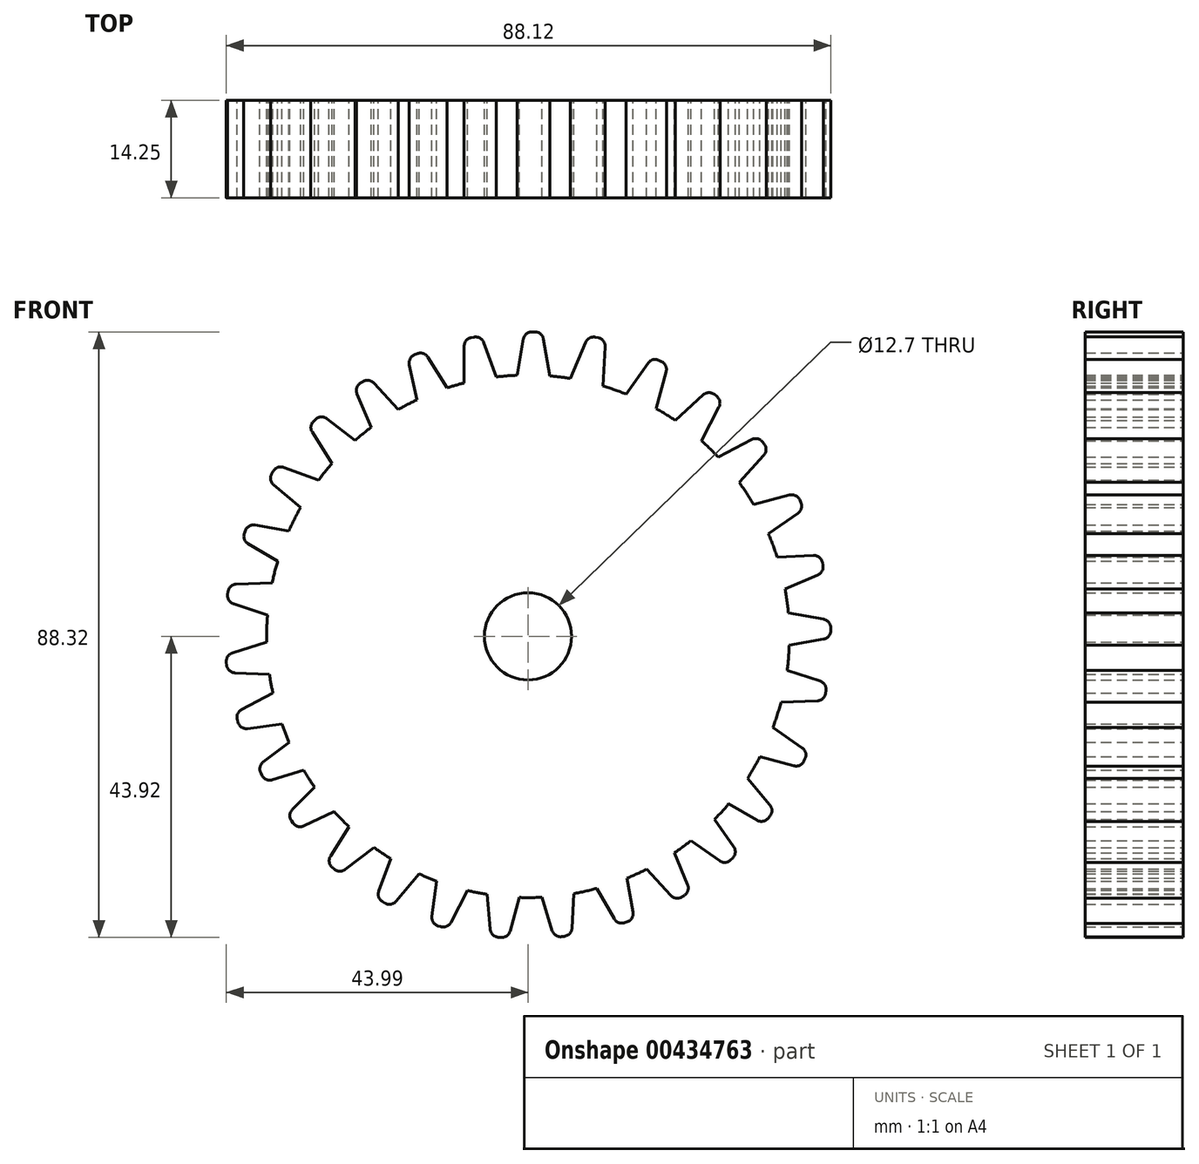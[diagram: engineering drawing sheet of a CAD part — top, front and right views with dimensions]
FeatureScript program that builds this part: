
annotation { "Feature Type Name" : "Feature", "Feature Type Description" : "" }
export const myFeature = defineFeature(function(context is Context, id is Id, definition is map)
    precondition{}
    {
        {
            var Q0;
            Q0=qCreatedBy(makeId("Front.planeOp"),FACE);
            var sketch = newSketch(context, id + "F0", { "sketchPlane" : qUnion([Q0])});
            skCircle(sketch, "E0", {"center": v(0, 0) * mm, "radius": 38.1 * mm});
            skCircle(sketch, "E1", {"center": v(0, 0) * mm, "radius": 6.35 * mm});
            skSolve(sketch);
        }
        {
            var Q0;
            Q0=makeQuery(id+"F0.imprint","IMPRINT",FACE,{"disambiguationData":[TD([[makeQuery(id+"F0.imprint","IMPRINT",EDGE,{"derivedFrom":sQuery(id+"F0.wireOp",EDGE,"E0")}),1.0]])]});
            extrude(context, id + "F1", {"entities" : qUnion([Q0]), "depth" : 7.87 * mm});
        }
        {
            var Q0;
            Q0=qCreatedBy(makeId("Front.planeOp"),FACE);
            var sketch = newSketch(context, id + "F2", { "sketchPlane" : qUnion([Q0])});
            skLineSegment(sketch, "E2", {"start": v(-58, 24.58) * mm, "end": v(-57.59, 24.58) * mm});
            skLineSegment(sketch, "E3", {"start": v(-56.34, 23.53) * mm, "end": v(-55.23, 17.27) * mm});
            skLineSegment(sketch, "E4", {"start": v(-55.23, 17.27) * mm, "end": v(-60.35, 17.27) * mm});
            skLineSegment(sketch, "E5", {"start": v(-59.25, 23.53) * mm, "end": v(-60.35, 17.27) * mm});
            skPoint(sketch, "E6.visualSharp", {"position": v(-59.06, 24.58) * mm});
            skArc(sketch, "E6.filletArc", {"start": v(-58, 24.58) * mm, "mid": v(-58.81, 24.29) * mm, "end": v(-59.25, 23.53) * mm});
            skPoint(sketch, "E7.visualSharp", {"position": v(-56.52, 24.58) * mm});
            skArc(sketch, "E7.filletArc", {"start": v(-56.34, 23.53) * mm, "mid": v(-56.77, 24.29) * mm, "end": v(-57.59, 24.58) * mm});
            skLineSegment(sketch, "E8", {"start": v(9.87, 43.61) * mm, "end": v(10.27, 43.52) * mm});
            skLineSegment(sketch, "E9", {"start": v(11.25, 42.22) * mm, "end": v(10.92, 35.86) * mm});
            skLineSegment(sketch, "E10", {"start": v(10.92, 35.86) * mm, "end": v(5.93, 37.01) * mm});
            skLineSegment(sketch, "E11", {"start": v(8.42, 42.87) * mm, "end": v(5.93, 37.01) * mm});
            skArc(sketch, "E12.filletArc", {"start": v(9.87, 43.61) * mm, "mid": v(9, 43.5) * mm, "end": v(8.42, 42.87) * mm});
            skArc(sketch, "E13.filletArc", {"start": v(11.25, 42.22) * mm, "mid": v(11, 43.05) * mm, "end": v(10.27, 43.52) * mm});
            skLineSegment(sketch, "E14", {"start": v(19.08, 40.25) * mm, "end": v(19.45, 40.08) * mm});
            skLineSegment(sketch, "E15", {"start": v(20.13, 38.6) * mm, "end": v(18.44, 32.46) * mm});
            skLineSegment(sketch, "E16", {"start": v(18.44, 32.46) * mm, "end": v(13.81, 34.66) * mm});
            skLineSegment(sketch, "E17", {"start": v(17.5, 39.84) * mm, "end": v(13.81, 34.66) * mm});
            skArc(sketch, "E18.filletArc", {"start": v(19.08, 40.25) * mm, "mid": v(18.21, 40.34) * mm, "end": v(17.5, 39.84) * mm});
            skArc(sketch, "E19.filletArc", {"start": v(20.13, 38.6) * mm, "mid": v(20.06, 39.46) * mm, "end": v(19.45, 40.08) * mm});
            skLineSegment(sketch, "E20", {"start": v(27.15, 35.27) * mm, "end": v(27.48, 35.03) * mm});
            skLineSegment(sketch, "E21", {"start": v(27.84, 33.43) * mm, "end": v(24.91, 27.78) * mm});
            skLineSegment(sketch, "E22", {"start": v(24.91, 27.78) * mm, "end": v(20.84, 30.88) * mm});
            skLineSegment(sketch, "E23", {"start": v(25.52, 35.2) * mm, "end": v(20.84, 30.88) * mm});
            skArc(sketch, "E24.filletArc", {"start": v(27.15, 35.27) * mm, "mid": v(26.32, 35.53) * mm, "end": v(25.52, 35.2) * mm});
            skArc(sketch, "E25.filletArc", {"start": v(27.84, 33.43) * mm, "mid": v(27.95, 34.3) * mm, "end": v(27.48, 35.03) * mm});
            skLineSegment(sketch, "E26", {"start": v(34.19, 28.35) * mm, "end": v(34.44, 28.03) * mm});
            skLineSegment(sketch, "E27", {"start": v(34.38, 26.4) * mm, "end": v(30.1, 21.68) * mm});
            skLineSegment(sketch, "E28", {"start": v(30.1, 21.68) * mm, "end": v(26.97, 25.73) * mm});
            skLineSegment(sketch, "E29", {"start": v(32.6, 28.7) * mm, "end": v(26.97, 25.73) * mm});
            skArc(sketch, "E30.filletArc", {"start": v(34.19, 28.35) * mm, "mid": v(33.45, 28.82) * mm, "end": v(32.6, 28.7) * mm});
            skArc(sketch, "E31.filletArc", {"start": v(34.38, 26.4) * mm, "mid": v(34.7, 27.2) * mm, "end": v(34.44, 28.03) * mm});
            skLineSegment(sketch, "E32", {"start": v(39.6, 19.9) * mm, "end": v(39.77, 19.53) * mm});
            skLineSegment(sketch, "E33", {"start": v(39.35, 17.96) * mm, "end": v(34.14, 14.3) * mm});
            skLineSegment(sketch, "E34", {"start": v(34.14, 14.3) * mm, "end": v(31.97, 18.95) * mm});
            skLineSegment(sketch, "E35", {"start": v(38.12, 20.6) * mm, "end": v(31.97, 18.95) * mm});
            skArc(sketch, "E36.filletArc", {"start": v(39.6, 19.9) * mm, "mid": v(38.98, 20.52) * mm, "end": v(38.12, 20.6) * mm});
            skArc(sketch, "E37.filletArc", {"start": v(39.35, 17.96) * mm, "mid": v(39.85, 18.67) * mm, "end": v(39.77, 19.53) * mm});
            skLineSegment(sketch, "E38", {"start": v(42.9, 10.8) * mm, "end": v(43, 10.4) * mm});
            skLineSegment(sketch, "E39", {"start": v(42.25, 8.95) * mm, "end": v(36.4, 6.47) * mm});
            skLineSegment(sketch, "E40", {"start": v(36.4, 6.47) * mm, "end": v(35.24, 11.46) * mm});
            skLineSegment(sketch, "E41", {"start": v(41.6, 11.79) * mm, "end": v(35.24, 11.46) * mm});
            skArc(sketch, "E42.filletArc", {"start": v(42.9, 10.8) * mm, "mid": v(42.43, 11.53) * mm, "end": v(41.6, 11.79) * mm});
            skArc(sketch, "E43.filletArc", {"start": v(42.25, 8.95) * mm, "mid": v(42.89, 9.54) * mm, "end": v(43, 10.4) * mm});
            skLineSegment(sketch, "E44", {"start": v(44.13, 1.24) * mm, "end": v(44.13, 0.83) * mm});
            skLineSegment(sketch, "E45", {"start": v(43.08, -0.42) * mm, "end": v(36.82, -1.52) * mm});
            skLineSegment(sketch, "E46", {"start": v(36.82, -1.52) * mm, "end": v(36.82, 3.6) * mm});
            skLineSegment(sketch, "E47", {"start": v(43.08, 2.5) * mm, "end": v(36.82, 3.6) * mm});
            skArc(sketch, "E48.filletArc", {"start": v(44.13, 1.24) * mm, "mid": v(43.84, 2.06) * mm, "end": v(43.08, 2.5) * mm});
            skArc(sketch, "E49.filletArc", {"start": v(43.08, -0.42) * mm, "mid": v(43.84, 0.02) * mm, "end": v(44.13, 0.83) * mm});
            skLineSegment(sketch, "E50", {"start": v(43.43, -7.9) * mm, "end": v(43.38, -8.31) * mm});
            skLineSegment(sketch, "E51", {"start": v(42.17, -9.4) * mm, "end": v(35.8, -9.64) * mm});
            skLineSegment(sketch, "E52", {"start": v(35.8, -9.64) * mm, "end": v(36.51, -4.57) * mm});
            skLineSegment(sketch, "E53", {"start": v(42.57, -6.52) * mm, "end": v(36.51, -4.57) * mm});
            skArc(sketch, "E54.filletArc", {"start": v(43.43, -7.9) * mm, "mid": v(43.25, -7.06) * mm, "end": v(42.57, -6.52) * mm});
            skArc(sketch, "E55.filletArc", {"start": v(42.17, -9.4) * mm, "mid": v(42.97, -9.08) * mm, "end": v(43.38, -8.31) * mm});
            skLineSegment(sketch, "E56", {"start": v(40.4, -17.82) * mm, "end": v(40.22, -18.2) * mm});
            skLineSegment(sketch, "E57", {"start": v(38.74, -18.88) * mm, "end": v(32.6, -17.24) * mm});
            skLineSegment(sketch, "E58", {"start": v(32.6, -17.24) * mm, "end": v(34.76, -12.6) * mm});
            skLineSegment(sketch, "E59", {"start": v(39.97, -16.25) * mm, "end": v(34.76, -12.6) * mm});
            skArc(sketch, "E60.filletArc", {"start": v(40.4, -17.82) * mm, "mid": v(40.47, -16.96) * mm, "end": v(39.97, -16.25) * mm});
            skArc(sketch, "E61.filletArc", {"start": v(38.74, -18.88) * mm, "mid": v(39.6, -18.8) * mm, "end": v(40.22, -18.2) * mm});
            skLineSegment(sketch, "E62", {"start": v(35.25, -26.23) * mm, "end": v(35, -26.54) * mm});
            skLineSegment(sketch, "E63", {"start": v(33.38, -26.82) * mm, "end": v(27.87, -23.64) * mm});
            skLineSegment(sketch, "E64", {"start": v(27.87, -23.64) * mm, "end": v(31.16, -19.72) * mm});
            skLineSegment(sketch, "E65", {"start": v(35.25, -24.6) * mm, "end": v(31.16, -19.72) * mm});
            skArc(sketch, "E66.filletArc", {"start": v(35.25, -26.23) * mm, "mid": v(35.55, -25.4) * mm, "end": v(35.25, -24.6) * mm});
            skArc(sketch, "E67.filletArc", {"start": v(33.38, -26.82) * mm, "mid": v(34.24, -26.97) * mm, "end": v(35, -26.54) * mm});
            skLineSegment(sketch, "E68", {"start": v(29.84, -32.3) * mm, "end": v(29.55, -32.6) * mm});
            skLineSegment(sketch, "E69", {"start": v(27.92, -32.74) * mm, "end": v(22.71, -29.1) * mm});
            skLineSegment(sketch, "E70", {"start": v(22.71, -29.1) * mm, "end": v(26.33, -25.47) * mm});
            skLineSegment(sketch, "E71", {"start": v(29.98, -30.68) * mm, "end": v(26.33, -25.47) * mm});
            skArc(sketch, "E72.filletArc", {"start": v(29.84, -32.3) * mm, "mid": v(30.2, -31.52) * mm, "end": v(29.98, -30.68) * mm});
            skArc(sketch, "E73.filletArc", {"start": v(27.92, -32.74) * mm, "mid": v(28.76, -32.97) * mm, "end": v(29.55, -32.6) * mm});
            skLineSegment(sketch, "E74", {"start": v(22.78, -37.77) * mm, "end": v(22.44, -38) * mm});
            skLineSegment(sketch, "E75", {"start": v(20.82, -37.78) * mm, "end": v(16.5, -33.11) * mm});
            skLineSegment(sketch, "E76", {"start": v(16.5, -33.11) * mm, "end": v(20.8, -30.34) * mm});
            skLineSegment(sketch, "E77", {"start": v(23.27, -36.21) * mm, "end": v(20.8, -30.34) * mm});
            skArc(sketch, "E78.filletArc", {"start": v(22.78, -37.77) * mm, "mid": v(23.3, -37.08) * mm, "end": v(23.27, -36.21) * mm});
            skArc(sketch, "E79.filletArc", {"start": v(20.82, -37.78) * mm, "mid": v(21.6, -38.18) * mm, "end": v(22.44, -38) * mm});
            skLineSegment(sketch, "E80", {"start": v(14.49, -41.62) * mm, "end": v(14.1, -41.76) * mm});
            skLineSegment(sketch, "E81", {"start": v(12.57, -41.2) * mm, "end": v(9.4, -35.68) * mm});
            skLineSegment(sketch, "E82", {"start": v(9.4, -35.68) * mm, "end": v(14.21, -33.94) * mm});
            skLineSegment(sketch, "E83", {"start": v(15.3, -40.2) * mm, "end": v(14.21, -33.94) * mm});
            skArc(sketch, "E84.filletArc", {"start": v(14.49, -41.62) * mm, "mid": v(15.16, -41.06) * mm, "end": v(15.3, -40.2) * mm});
            skArc(sketch, "E85.filletArc", {"start": v(12.57, -41.2) * mm, "mid": v(13.24, -41.75) * mm, "end": v(14.1, -41.76) * mm});
            skLineSegment(sketch, "E86", {"start": v(5.3, -43.74) * mm, "end": v(4.89, -43.8) * mm});
            skLineSegment(sketch, "E87", {"start": v(3.52, -42.91) * mm, "end": v(1.63, -36.84) * mm});
            skLineSegment(sketch, "E88", {"start": v(1.63, -36.84) * mm, "end": v(6.7, -36.19) * mm});
            skLineSegment(sketch, "E89", {"start": v(6.4, -42.54) * mm, "end": v(6.7, -36.19) * mm});
            skArc(sketch, "E90.filletArc", {"start": v(5.3, -43.74) * mm, "mid": v(6.07, -43.35) * mm, "end": v(6.4, -42.54) * mm});
            skArc(sketch, "E91.filletArc", {"start": v(3.52, -42.91) * mm, "mid": v(4.04, -43.6) * mm, "end": v(4.89, -43.8) * mm});
            skLineSegment(sketch, "E92", {"start": v(-3.96, -43.91) * mm, "end": v(-4.37, -43.87) * mm});
            skLineSegment(sketch, "E93", {"start": v(-5.52, -42.71) * mm, "end": v(-6.04, -36.37) * mm});
            skLineSegment(sketch, "E94", {"start": v(-6.04, -36.37) * mm, "end": v(-0.95, -36.84) * mm});
            skLineSegment(sketch, "E95", {"start": v(-2.62, -42.98) * mm, "end": v(-0.95, -36.84) * mm});
            skArc(sketch, "E96.filletArc", {"start": v(-3.96, -43.91) * mm, "mid": v(-3.12, -43.69) * mm, "end": v(-2.62, -42.98) * mm});
            skArc(sketch, "E97.filletArc", {"start": v(-5.52, -42.71) * mm, "mid": v(-5.16, -43.5) * mm, "end": v(-4.37, -43.87) * mm});
            skLineSegment(sketch, "E98", {"start": v(-12.74, -42.34) * mm, "end": v(-13.13, -42.21) * mm});
            skLineSegment(sketch, "E99", {"start": v(-14.01, -40.84) * mm, "end": v(-13.18, -34.53) * mm});
            skLineSegment(sketch, "E100", {"start": v(-13.18, -34.53) * mm, "end": v(-8.3, -36.07) * mm});
            skLineSegment(sketch, "E101", {"start": v(-11.24, -41.71) * mm, "end": v(-8.3, -36.07) * mm});
            skArc(sketch, "E102.filletArc", {"start": v(-12.74, -42.34) * mm, "mid": v(-11.88, -42.3) * mm, "end": v(-11.24, -41.71) * mm});
            skArc(sketch, "E103.filletArc", {"start": v(-14.01, -40.84) * mm, "mid": v(-13.82, -41.68) * mm, "end": v(-13.13, -42.21) * mm});
            skLineSegment(sketch, "E104", {"start": v(-20.84, -38.92) * mm, "end": v(-21.2, -38.72) * mm});
            skLineSegment(sketch, "E105", {"start": v(-21.76, -37.18) * mm, "end": v(-19.59, -31.2) * mm});
            skLineSegment(sketch, "E106", {"start": v(-19.59, -31.2) * mm, "end": v(-15.15, -33.75) * mm});
            skLineSegment(sketch, "E107", {"start": v(-19.23, -38.63) * mm, "end": v(-15.15, -33.75) * mm});
            skArc(sketch, "E108.filletArc", {"start": v(-20.84, -38.92) * mm, "mid": v(-19.99, -39.07) * mm, "end": v(-19.23, -38.63) * mm});
            skArc(sketch, "E109.filletArc", {"start": v(-21.76, -37.18) * mm, "mid": v(-21.76, -38.05) * mm, "end": v(-21.2, -38.72) * mm});
            skLineSegment(sketch, "E110", {"start": v(-28.28, -33.93) * mm, "end": v(-28.58, -33.66) * mm});
            skLineSegment(sketch, "E111", {"start": v(-28.8, -32.04) * mm, "end": v(-25.37, -26.67) * mm});
            skLineSegment(sketch, "E112", {"start": v(-25.37, -26.67) * mm, "end": v(-21.6, -30.13) * mm});
            skLineSegment(sketch, "E113", {"start": v(-26.65, -34) * mm, "end": v(-21.6, -30.13) * mm});
            skArc(sketch, "E114.filletArc", {"start": v(-28.28, -33.93) * mm, "mid": v(-27.48, -34.27) * mm, "end": v(-26.65, -34) * mm});
            skArc(sketch, "E115.filletArc", {"start": v(-28.8, -32.04) * mm, "mid": v(-28.98, -32.89) * mm, "end": v(-28.58, -33.66) * mm});
            skLineSegment(sketch, "E116", {"start": v(-34.27, -27.22) * mm, "end": v(-34.5, -26.88) * mm});
            skLineSegment(sketch, "E117", {"start": v(-34.36, -25.26) * mm, "end": v(-29.86, -20.76) * mm});
            skLineSegment(sketch, "E118", {"start": v(-29.86, -20.76) * mm, "end": v(-26.92, -24.95) * mm});
            skLineSegment(sketch, "E119", {"start": v(-32.7, -27.64) * mm, "end": v(-26.92, -24.95) * mm});
            skArc(sketch, "E120.filletArc", {"start": v(-34.27, -27.22) * mm, "mid": v(-33.56, -27.72) * mm, "end": v(-32.7, -27.64) * mm});
            skArc(sketch, "E121.filletArc", {"start": v(-34.36, -25.26) * mm, "mid": v(-34.73, -26.05) * mm, "end": v(-34.5, -26.88) * mm});
            skLineSegment(sketch, "E122", {"start": v(-38.77, -20.3) * mm, "end": v(-38.95, -19.93) * mm});
            skLineSegment(sketch, "E123", {"start": v(-38.6, -18.34) * mm, "end": v(-33.54, -14.48) * mm});
            skLineSegment(sketch, "E124", {"start": v(-33.54, -14.48) * mm, "end": v(-31.19, -19.02) * mm});
            skLineSegment(sketch, "E125", {"start": v(-37.26, -20.92) * mm, "end": v(-31.19, -19.02) * mm});
            skArc(sketch, "E126.filletArc", {"start": v(-38.77, -20.3) * mm, "mid": v(-38.13, -20.88) * mm, "end": v(-37.26, -20.92) * mm});
            skArc(sketch, "E127.filletArc", {"start": v(-38.6, -18.34) * mm, "mid": v(-39.07, -19.07) * mm, "end": v(-38.95, -19.93) * mm});
            skLineSegment(sketch, "E128", {"start": v(-42.26, -12.59) * mm, "end": v(-42.38, -12.2) * mm});
            skLineSegment(sketch, "E129", {"start": v(-41.77, -10.69) * mm, "end": v(-36.14, -7.72) * mm});
            skLineSegment(sketch, "E130", {"start": v(-36.14, -7.72) * mm, "end": v(-34.57, -12.59) * mm});
            skLineSegment(sketch, "E131", {"start": v(-40.87, -13.46) * mm, "end": v(-34.57, -12.59) * mm});
            skArc(sketch, "E132.filletArc", {"start": v(-42.26, -12.59) * mm, "mid": v(-41.72, -13.28) * mm, "end": v(-40.87, -13.46) * mm});
            skArc(sketch, "E133.filletArc", {"start": v(-41.77, -10.69) * mm, "mid": v(-42.35, -11.33) * mm, "end": v(-42.38, -12.2) * mm});
            skLineSegment(sketch, "E134", {"start": v(-43.93, -4.22) * mm, "end": v(-43.98, -3.82) * mm});
            skLineSegment(sketch, "E135", {"start": v(-43.1, -2.44) * mm, "end": v(-37.03, -0.54) * mm});
            skLineSegment(sketch, "E136", {"start": v(-37.03, -0.54) * mm, "end": v(-36.37, -5.61) * mm});
            skLineSegment(sketch, "E137", {"start": v(-42.72, -5.33) * mm, "end": v(-36.37, -5.61) * mm});
            skArc(sketch, "E138.filletArc", {"start": v(-43.93, -4.22) * mm, "mid": v(-43.53, -5) * mm, "end": v(-42.72, -5.33) * mm});
            skArc(sketch, "E139.filletArc", {"start": v(-43.1, -2.44) * mm, "mid": v(-43.8, -2.97) * mm, "end": v(-43.98, -3.82) * mm});
            skLineSegment(sketch, "E140", {"start": v(-43.79, 6.1) * mm, "end": v(-43.73, 6.5) * mm});
            skLineSegment(sketch, "E141", {"start": v(-42.52, 7.6) * mm, "end": v(-36.16, 7.84) * mm});
            skLineSegment(sketch, "E142", {"start": v(-36.16, 7.84) * mm, "end": v(-36.86, 2.77) * mm});
            skLineSegment(sketch, "E143", {"start": v(-42.92, 4.72) * mm, "end": v(-36.86, 2.77) * mm});
            skArc(sketch, "E144.filletArc", {"start": v(-43.79, 6.1) * mm, "mid": v(-43.6, 5.25) * mm, "end": v(-42.92, 4.72) * mm});
            skArc(sketch, "E145.filletArc", {"start": v(-42.52, 7.6) * mm, "mid": v(-43.32, 7.27) * mm, "end": v(-43.73, 6.5) * mm});
            skLineSegment(sketch, "E146", {"start": v(-41.36, 15.02) * mm, "end": v(-41.22, 15.4) * mm});
            skLineSegment(sketch, "E147", {"start": v(-39.8, 16.22) * mm, "end": v(-33.54, 15.12) * mm});
            skLineSegment(sketch, "E148", {"start": v(-33.54, 15.12) * mm, "end": v(-35.29, 10.3) * mm});
            skLineSegment(sketch, "E149", {"start": v(-40.8, 13.49) * mm, "end": v(-35.29, 10.3) * mm});
            skArc(sketch, "E150.filletArc", {"start": v(-41.36, 15.02) * mm, "mid": v(-41.36, 14.15) * mm, "end": v(-40.8, 13.49) * mm});
            skArc(sketch, "E151.filletArc", {"start": v(-39.8, 16.22) * mm, "mid": v(-40.66, 16.07) * mm, "end": v(-41.22, 15.4) * mm});
            skLineSegment(sketch, "E152", {"start": v(-37.37, 23.71) * mm, "end": v(-37.17, 24.06) * mm});
            skLineSegment(sketch, "E153", {"start": v(-35.63, 24.62) * mm, "end": v(-29.65, 22.45) * mm});
            skLineSegment(sketch, "E154", {"start": v(-29.65, 22.45) * mm, "end": v(-32.21, 18.01) * mm});
            skLineSegment(sketch, "E155", {"start": v(-37.09, 22.1) * mm, "end": v(-32.21, 18.01) * mm});
            skArc(sketch, "E156.filletArc", {"start": v(-37.37, 23.71) * mm, "mid": v(-37.52, 22.86) * mm, "end": v(-37.09, 22.1) * mm});
            skArc(sketch, "E157.filletArc", {"start": v(-35.63, 24.62) * mm, "mid": v(-36.5, 24.62) * mm, "end": v(-37.17, 24.06) * mm});
            skLineSegment(sketch, "E158", {"start": v(-31.25, 31.38) * mm, "end": v(-30.94, 31.66) * mm});
            skLineSegment(sketch, "E159", {"start": v(-29.31, 31.73) * mm, "end": v(-24.27, 27.85) * mm});
            skLineSegment(sketch, "E160", {"start": v(-24.27, 27.85) * mm, "end": v(-28.04, 24.4) * mm});
            skLineSegment(sketch, "E161", {"start": v(-31.46, 29.76) * mm, "end": v(-28.04, 24.4) * mm});
            skArc(sketch, "E162.filletArc", {"start": v(-31.25, 31.38) * mm, "mid": v(-31.65, 30.61) * mm, "end": v(-31.46, 29.76) * mm});
            skArc(sketch, "E163.filletArc", {"start": v(-29.31, 31.73) * mm, "mid": v(-30.14, 31.99) * mm, "end": v(-30.94, 31.66) * mm});
            skLineSegment(sketch, "E164", {"start": v(-24.43, 36.92) * mm, "end": v(-24.09, 37.14) * mm});
            skLineSegment(sketch, "E165", {"start": v(-22.47, 36.93) * mm, "end": v(-18.17, 32.24) * mm});
            skLineSegment(sketch, "E166", {"start": v(-18.17, 32.24) * mm, "end": v(-22.48, 29.49) * mm});
            skLineSegment(sketch, "E167", {"start": v(-24.92, 35.36) * mm, "end": v(-22.48, 29.49) * mm});
            skArc(sketch, "E168.filletArc", {"start": v(-24.43, 36.92) * mm, "mid": v(-24.96, 36.23) * mm, "end": v(-24.92, 35.36) * mm});
            skArc(sketch, "E169.filletArc", {"start": v(-22.47, 36.93) * mm, "mid": v(-23.24, 37.33) * mm, "end": v(-24.09, 37.14) * mm});
            skLineSegment(sketch, "E170", {"start": v(-16.54, 41.05) * mm, "end": v(-16.17, 41.2) * mm});
            skLineSegment(sketch, "E171", {"start": v(-14.61, 40.7) * mm, "end": v(-11.22, 35.32) * mm});
            skLineSegment(sketch, "E172", {"start": v(-11.22, 35.32) * mm, "end": v(-15.97, 33.4) * mm});
            skLineSegment(sketch, "E173", {"start": v(-17.3, 39.6) * mm, "end": v(-15.97, 33.4) * mm});
            skArc(sketch, "E174.filletArc", {"start": v(-16.54, 41.05) * mm, "mid": v(-17.19, 40.47) * mm, "end": v(-17.3, 39.6) * mm});
            skArc(sketch, "E175.filletArc", {"start": v(-14.61, 40.7) * mm, "mid": v(-15.3, 41.24) * mm, "end": v(-16.17, 41.2) * mm});
            skLineSegment(sketch, "E176", {"start": v(-8.26, 43.56) * mm, "end": v(-7.86, 43.64) * mm});
            skLineSegment(sketch, "E177", {"start": v(-6.45, 42.82) * mm, "end": v(-4.27, 36.84) * mm});
            skLineSegment(sketch, "E178", {"start": v(-4.27, 36.84) * mm, "end": v(-9.31, 35.95) * mm});
            skLineSegment(sketch, "E179", {"start": v(-9.31, 42.31) * mm, "end": v(-9.31, 35.95) * mm});
            skArc(sketch, "E180.filletArc", {"start": v(-8.26, 43.56) * mm, "mid": v(-9.02, 43.13) * mm, "end": v(-9.31, 42.31) * mm});
            skArc(sketch, "E181.filletArc", {"start": v(-6.45, 42.82) * mm, "mid": v(-7, 43.49) * mm, "end": v(-7.86, 43.64) * mm});
            skLineSegment(sketch, "E182", {"start": v(0.58, 44.4) * mm, "end": v(0.99, 44.4) * mm});
            skLineSegment(sketch, "E183", {"start": v(2.24, 43.35) * mm, "end": v(3.34, 37.08) * mm});
            skLineSegment(sketch, "E184", {"start": v(3.34, 37.08) * mm, "end": v(-1.78, 37.08) * mm});
            skLineSegment(sketch, "E185", {"start": v(-0.67, 43.35) * mm, "end": v(-1.78, 37.08) * mm});
            skArc(sketch, "E186.filletArc", {"start": v(0.58, 44.4) * mm, "mid": v(-0.24, 44.1) * mm, "end": v(-0.67, 43.35) * mm});
            skArc(sketch, "E187.filletArc", {"start": v(2.24, 43.35) * mm, "mid": v(1.8, 44.1) * mm, "end": v(0.99, 44.4) * mm});
            skSolve(sketch);
        }
        {
            var Q0;
            Q0 = qSketchRegion(id + "F2", true);
            extrude(context, id + "F3", {"entities" : qUnion([Q0]), "operationType" : NewBodyOperationType.ADD, "depth" : 7.82 * mm});
        }
        {
            var Q0;
            Q0=makeQuery(id+"F3.opExtrude","SWEPT_BODY",BODY,{"disambiguationData":[OSD([sQuery(id+"F2.wireOp",EDGE,"E2"),sQuery(id+"F2.wireOp",EDGE,"E3"),sQuery(id+"F2.wireOp",EDGE,"E4"),sQuery(id+"F2.wireOp",EDGE,"E5"),sQuery(id+"F2.wireOp",EDGE,"E6.filletArc"),sQuery(id+"F2.wireOp",EDGE,"E7.filletArc")])]});
            deleteBodies(context, id + "F4", {"entities" : qUnion([Q0])});
        }
        {
            var Q0;
            Q0 = qSketchRegion(id + "F2", true);
            extrude(context, id + "F5", {"entities" : qUnion([Q0]), "operationType" : NewBodyOperationType.ADD, "depth" : 7.04 * mm});
        }
        {
            var Q0;
            Q0=makeQuery(id+"F5.opExtrude","SWEPT_BODY",BODY,{"disambiguationData":[OSD([sQuery(id+"F2.wireOp",EDGE,"E2"),sQuery(id+"F2.wireOp",EDGE,"E3"),sQuery(id+"F2.wireOp",EDGE,"E4"),sQuery(id+"F2.wireOp",EDGE,"E5"),sQuery(id+"F2.wireOp",EDGE,"E6.filletArc"),sQuery(id+"F2.wireOp",EDGE,"E7.filletArc")])]});
            deleteBodies(context, id + "F6", {"entities" : qUnion([Q0])});
        }
        {
            var Q0;
            Q0=makeQuery(id+"F1.opExtrude","CAP_FACE",FACE,{"disambiguationData":[OSD([sQuery(id+"F0.wireOp",EDGE,"E0"),sQuery(id+"F0.wireOp",EDGE,"E1")])],"isStart":false});
            extrude(context, id + "F7", {"entities" : qUnion([Q0]), "operationType" : NewBodyOperationType.ADD, "depth" : 6.35 * mm});
        }
        {
            var Q0;
            Q0=makeQuery(id+"F3.boolean.opBoolean","MERGE",FACE,{"derivedFrom":[makeQuery(id+"F1.opExtrude","CAP_FACE",FACE,{"disambiguationData":[OSD([sQuery(id+"F0.wireOp",EDGE,"E0"),sQuery(id+"F0.wireOp",EDGE,"E1")])],"isStart":true}),makeQuery(id+"F3.opExtrude","CAP_FACE",FACE,{"disambiguationData":[OSD([sQuery(id+"F2.wireOp",EDGE,"E8"),sQuery(id+"F2.wireOp",EDGE,"E9"),sQuery(id+"F2.wireOp",EDGE,"E10"),sQuery(id+"F2.wireOp",EDGE,"E11"),sQuery(id+"F2.wireOp",EDGE,"E12.filletArc"),sQuery(id+"F2.wireOp",EDGE,"E13.filletArc")])],"isStart":true}),makeQuery(id+"F3.opExtrude","CAP_FACE",FACE,{"disambiguationData":[OSD([sQuery(id+"F2.wireOp",EDGE,"E14"),sQuery(id+"F2.wireOp",EDGE,"E15"),sQuery(id+"F2.wireOp",EDGE,"E16"),sQuery(id+"F2.wireOp",EDGE,"E17"),sQuery(id+"F2.wireOp",EDGE,"E18.filletArc"),sQuery(id+"F2.wireOp",EDGE,"E19.filletArc")])],"isStart":true}),makeQuery(id+"F3.opExtrude","CAP_FACE",FACE,{"disambiguationData":[OSD([sQuery(id+"F2.wireOp",EDGE,"E20"),sQuery(id+"F2.wireOp",EDGE,"E21"),sQuery(id+"F2.wireOp",EDGE,"E22"),sQuery(id+"F2.wireOp",EDGE,"E23"),sQuery(id+"F2.wireOp",EDGE,"E24.filletArc"),sQuery(id+"F2.wireOp",EDGE,"E25.filletArc")])],"isStart":true}),makeQuery(id+"F3.opExtrude","CAP_FACE",FACE,{"disambiguationData":[OSD([sQuery(id+"F2.wireOp",EDGE,"E26"),sQuery(id+"F2.wireOp",EDGE,"E27"),sQuery(id+"F2.wireOp",EDGE,"E28"),sQuery(id+"F2.wireOp",EDGE,"E29"),sQuery(id+"F2.wireOp",EDGE,"E30.filletArc"),sQuery(id+"F2.wireOp",EDGE,"E31.filletArc")])],"isStart":true}),makeQuery(id+"F3.opExtrude","CAP_FACE",FACE,{"disambiguationData":[OSD([sQuery(id+"F2.wireOp",EDGE,"E32"),sQuery(id+"F2.wireOp",EDGE,"E33"),sQuery(id+"F2.wireOp",EDGE,"E34"),sQuery(id+"F2.wireOp",EDGE,"E35"),sQuery(id+"F2.wireOp",EDGE,"E36.filletArc"),sQuery(id+"F2.wireOp",EDGE,"E37.filletArc")])],"isStart":true}),makeQuery(id+"F3.opExtrude","CAP_FACE",FACE,{"disambiguationData":[OSD([sQuery(id+"F2.wireOp",EDGE,"E38"),sQuery(id+"F2.wireOp",EDGE,"E39"),sQuery(id+"F2.wireOp",EDGE,"E40"),sQuery(id+"F2.wireOp",EDGE,"E41"),sQuery(id+"F2.wireOp",EDGE,"E42.filletArc"),sQuery(id+"F2.wireOp",EDGE,"E43.filletArc")])],"isStart":true}),makeQuery(id+"F3.opExtrude","CAP_FACE",FACE,{"disambiguationData":[OSD([sQuery(id+"F2.wireOp",EDGE,"E44"),sQuery(id+"F2.wireOp",EDGE,"E45"),sQuery(id+"F2.wireOp",EDGE,"E46"),sQuery(id+"F2.wireOp",EDGE,"E47"),sQuery(id+"F2.wireOp",EDGE,"E48.filletArc"),sQuery(id+"F2.wireOp",EDGE,"E49.filletArc")])],"isStart":true}),makeQuery(id+"F3.opExtrude","CAP_FACE",FACE,{"disambiguationData":[OSD([sQuery(id+"F2.wireOp",EDGE,"E50"),sQuery(id+"F2.wireOp",EDGE,"E51"),sQuery(id+"F2.wireOp",EDGE,"E52"),sQuery(id+"F2.wireOp",EDGE,"E53"),sQuery(id+"F2.wireOp",EDGE,"E54.filletArc"),sQuery(id+"F2.wireOp",EDGE,"E55.filletArc")])],"isStart":true}),makeQuery(id+"F3.opExtrude","CAP_FACE",FACE,{"disambiguationData":[OSD([sQuery(id+"F2.wireOp",EDGE,"E56"),sQuery(id+"F2.wireOp",EDGE,"E57"),sQuery(id+"F2.wireOp",EDGE,"E58"),sQuery(id+"F2.wireOp",EDGE,"E59"),sQuery(id+"F2.wireOp",EDGE,"E60.filletArc"),sQuery(id+"F2.wireOp",EDGE,"E61.filletArc")])],"isStart":true}),makeQuery(id+"F3.opExtrude","CAP_FACE",FACE,{"disambiguationData":[OSD([sQuery(id+"F2.wireOp",EDGE,"E62"),sQuery(id+"F2.wireOp",EDGE,"E63"),sQuery(id+"F2.wireOp",EDGE,"E64"),sQuery(id+"F2.wireOp",EDGE,"E65"),sQuery(id+"F2.wireOp",EDGE,"E66.filletArc"),sQuery(id+"F2.wireOp",EDGE,"E67.filletArc")])],"isStart":true}),makeQuery(id+"F3.opExtrude","CAP_FACE",FACE,{"disambiguationData":[OSD([sQuery(id+"F2.wireOp",EDGE,"E68"),sQuery(id+"F2.wireOp",EDGE,"E69"),sQuery(id+"F2.wireOp",EDGE,"E70"),sQuery(id+"F2.wireOp",EDGE,"E71"),sQuery(id+"F2.wireOp",EDGE,"E72.filletArc"),sQuery(id+"F2.wireOp",EDGE,"E73.filletArc")])],"isStart":true}),makeQuery(id+"F3.opExtrude","CAP_FACE",FACE,{"disambiguationData":[OSD([sQuery(id+"F2.wireOp",EDGE,"E74"),sQuery(id+"F2.wireOp",EDGE,"E75"),sQuery(id+"F2.wireOp",EDGE,"E76"),sQuery(id+"F2.wireOp",EDGE,"E77"),sQuery(id+"F2.wireOp",EDGE,"E78.filletArc"),sQuery(id+"F2.wireOp",EDGE,"E79.filletArc")])],"isStart":true}),makeQuery(id+"F3.opExtrude","CAP_FACE",FACE,{"disambiguationData":[OSD([sQuery(id+"F2.wireOp",EDGE,"E80"),sQuery(id+"F2.wireOp",EDGE,"E81"),sQuery(id+"F2.wireOp",EDGE,"E82"),sQuery(id+"F2.wireOp",EDGE,"E83"),sQuery(id+"F2.wireOp",EDGE,"E84.filletArc"),sQuery(id+"F2.wireOp",EDGE,"E85.filletArc")])],"isStart":true}),makeQuery(id+"F3.opExtrude","CAP_FACE",FACE,{"disambiguationData":[OSD([sQuery(id+"F2.wireOp",EDGE,"E86"),sQuery(id+"F2.wireOp",EDGE,"E87"),sQuery(id+"F2.wireOp",EDGE,"E88"),sQuery(id+"F2.wireOp",EDGE,"E89"),sQuery(id+"F2.wireOp",EDGE,"E90.filletArc"),sQuery(id+"F2.wireOp",EDGE,"E91.filletArc")])],"isStart":true}),makeQuery(id+"F3.opExtrude","CAP_FACE",FACE,{"disambiguationData":[OSD([sQuery(id+"F2.wireOp",EDGE,"E92"),sQuery(id+"F2.wireOp",EDGE,"E93"),sQuery(id+"F2.wireOp",EDGE,"E94"),sQuery(id+"F2.wireOp",EDGE,"E95"),sQuery(id+"F2.wireOp",EDGE,"E96.filletArc"),sQuery(id+"F2.wireOp",EDGE,"E97.filletArc")])],"isStart":true}),makeQuery(id+"F3.opExtrude","CAP_FACE",FACE,{"disambiguationData":[OSD([sQuery(id+"F2.wireOp",EDGE,"E98"),sQuery(id+"F2.wireOp",EDGE,"E99"),sQuery(id+"F2.wireOp",EDGE,"E100"),sQuery(id+"F2.wireOp",EDGE,"E101"),sQuery(id+"F2.wireOp",EDGE,"E102.filletArc"),sQuery(id+"F2.wireOp",EDGE,"E103.filletArc")])],"isStart":true}),makeQuery(id+"F3.opExtrude","CAP_FACE",FACE,{"disambiguationData":[OSD([sQuery(id+"F2.wireOp",EDGE,"E104"),sQuery(id+"F2.wireOp",EDGE,"E105"),sQuery(id+"F2.wireOp",EDGE,"E106"),sQuery(id+"F2.wireOp",EDGE,"E107"),sQuery(id+"F2.wireOp",EDGE,"E108.filletArc"),sQuery(id+"F2.wireOp",EDGE,"E109.filletArc")])],"isStart":true}),makeQuery(id+"F3.opExtrude","CAP_FACE",FACE,{"disambiguationData":[OSD([sQuery(id+"F2.wireOp",EDGE,"E110"),sQuery(id+"F2.wireOp",EDGE,"E111"),sQuery(id+"F2.wireOp",EDGE,"E112"),sQuery(id+"F2.wireOp",EDGE,"E113"),sQuery(id+"F2.wireOp",EDGE,"E114.filletArc"),sQuery(id+"F2.wireOp",EDGE,"E115.filletArc")])],"isStart":true}),makeQuery(id+"F3.opExtrude","CAP_FACE",FACE,{"disambiguationData":[OSD([sQuery(id+"F2.wireOp",EDGE,"E116"),sQuery(id+"F2.wireOp",EDGE,"E117"),sQuery(id+"F2.wireOp",EDGE,"E118"),sQuery(id+"F2.wireOp",EDGE,"E119"),sQuery(id+"F2.wireOp",EDGE,"E120.filletArc"),sQuery(id+"F2.wireOp",EDGE,"E121.filletArc")])],"isStart":true}),makeQuery(id+"F3.opExtrude","CAP_FACE",FACE,{"disambiguationData":[OSD([sQuery(id+"F2.wireOp",EDGE,"E122"),sQuery(id+"F2.wireOp",EDGE,"E123"),sQuery(id+"F2.wireOp",EDGE,"E124"),sQuery(id+"F2.wireOp",EDGE,"E125"),sQuery(id+"F2.wireOp",EDGE,"E126.filletArc"),sQuery(id+"F2.wireOp",EDGE,"E127.filletArc")])],"isStart":true}),makeQuery(id+"F3.opExtrude","CAP_FACE",FACE,{"disambiguationData":[OSD([sQuery(id+"F2.wireOp",EDGE,"E128"),sQuery(id+"F2.wireOp",EDGE,"E129"),sQuery(id+"F2.wireOp",EDGE,"E130"),sQuery(id+"F2.wireOp",EDGE,"E131"),sQuery(id+"F2.wireOp",EDGE,"E132.filletArc"),sQuery(id+"F2.wireOp",EDGE,"E133.filletArc")])],"isStart":true}),makeQuery(id+"F3.opExtrude","CAP_FACE",FACE,{"disambiguationData":[OSD([sQuery(id+"F2.wireOp",EDGE,"E134"),sQuery(id+"F2.wireOp",EDGE,"E135"),sQuery(id+"F2.wireOp",EDGE,"E136"),sQuery(id+"F2.wireOp",EDGE,"E137"),sQuery(id+"F2.wireOp",EDGE,"E138.filletArc"),sQuery(id+"F2.wireOp",EDGE,"E139.filletArc")])],"isStart":true}),makeQuery(id+"F3.opExtrude","CAP_FACE",FACE,{"disambiguationData":[OSD([sQuery(id+"F2.wireOp",EDGE,"E140"),sQuery(id+"F2.wireOp",EDGE,"E141"),sQuery(id+"F2.wireOp",EDGE,"E142"),sQuery(id+"F2.wireOp",EDGE,"E143"),sQuery(id+"F2.wireOp",EDGE,"E144.filletArc"),sQuery(id+"F2.wireOp",EDGE,"E145.filletArc")])],"isStart":true}),makeQuery(id+"F3.opExtrude","CAP_FACE",FACE,{"disambiguationData":[OSD([sQuery(id+"F2.wireOp",EDGE,"E146"),sQuery(id+"F2.wireOp",EDGE,"E147"),sQuery(id+"F2.wireOp",EDGE,"E148"),sQuery(id+"F2.wireOp",EDGE,"E149"),sQuery(id+"F2.wireOp",EDGE,"E150.filletArc"),sQuery(id+"F2.wireOp",EDGE,"E151.filletArc")])],"isStart":true}),makeQuery(id+"F3.opExtrude","CAP_FACE",FACE,{"disambiguationData":[OSD([sQuery(id+"F2.wireOp",EDGE,"E152"),sQuery(id+"F2.wireOp",EDGE,"E153"),sQuery(id+"F2.wireOp",EDGE,"E154"),sQuery(id+"F2.wireOp",EDGE,"E155"),sQuery(id+"F2.wireOp",EDGE,"E156.filletArc"),sQuery(id+"F2.wireOp",EDGE,"E157.filletArc")])],"isStart":true}),makeQuery(id+"F3.opExtrude","CAP_FACE",FACE,{"disambiguationData":[OSD([sQuery(id+"F2.wireOp",EDGE,"E158"),sQuery(id+"F2.wireOp",EDGE,"E159"),sQuery(id+"F2.wireOp",EDGE,"E160"),sQuery(id+"F2.wireOp",EDGE,"E161"),sQuery(id+"F2.wireOp",EDGE,"E162.filletArc"),sQuery(id+"F2.wireOp",EDGE,"E163.filletArc")])],"isStart":true}),makeQuery(id+"F3.opExtrude","CAP_FACE",FACE,{"disambiguationData":[OSD([sQuery(id+"F2.wireOp",EDGE,"E164"),sQuery(id+"F2.wireOp",EDGE,"E165"),sQuery(id+"F2.wireOp",EDGE,"E166"),sQuery(id+"F2.wireOp",EDGE,"E167"),sQuery(id+"F2.wireOp",EDGE,"E168.filletArc"),sQuery(id+"F2.wireOp",EDGE,"E169.filletArc")])],"isStart":true}),makeQuery(id+"F3.opExtrude","CAP_FACE",FACE,{"disambiguationData":[OSD([sQuery(id+"F2.wireOp",EDGE,"E170"),sQuery(id+"F2.wireOp",EDGE,"E171"),sQuery(id+"F2.wireOp",EDGE,"E172"),sQuery(id+"F2.wireOp",EDGE,"E173"),sQuery(id+"F2.wireOp",EDGE,"E174.filletArc"),sQuery(id+"F2.wireOp",EDGE,"E175.filletArc")])],"isStart":true}),makeQuery(id+"F3.opExtrude","CAP_FACE",FACE,{"disambiguationData":[OSD([sQuery(id+"F2.wireOp",EDGE,"E176"),sQuery(id+"F2.wireOp",EDGE,"E177"),sQuery(id+"F2.wireOp",EDGE,"E178"),sQuery(id+"F2.wireOp",EDGE,"E179"),sQuery(id+"F2.wireOp",EDGE,"E180.filletArc"),sQuery(id+"F2.wireOp",EDGE,"E181.filletArc")])],"isStart":true}),makeQuery(id+"F3.opExtrude","CAP_FACE",FACE,{"disambiguationData":[OSD([sQuery(id+"F2.wireOp",EDGE,"E182"),sQuery(id+"F2.wireOp",EDGE,"E183"),sQuery(id+"F2.wireOp",EDGE,"E184"),sQuery(id+"F2.wireOp",EDGE,"E185"),sQuery(id+"F2.wireOp",EDGE,"E186.filletArc"),sQuery(id+"F2.wireOp",EDGE,"E187.filletArc")])],"isStart":true})]});
            extrude(context, id + "F8", {"entities" : qUnion([Q0]), "operationType" : NewBodyOperationType.ADD, "oppositeDirection" : true, "depth" : 14.25 * mm});
        }
    });
